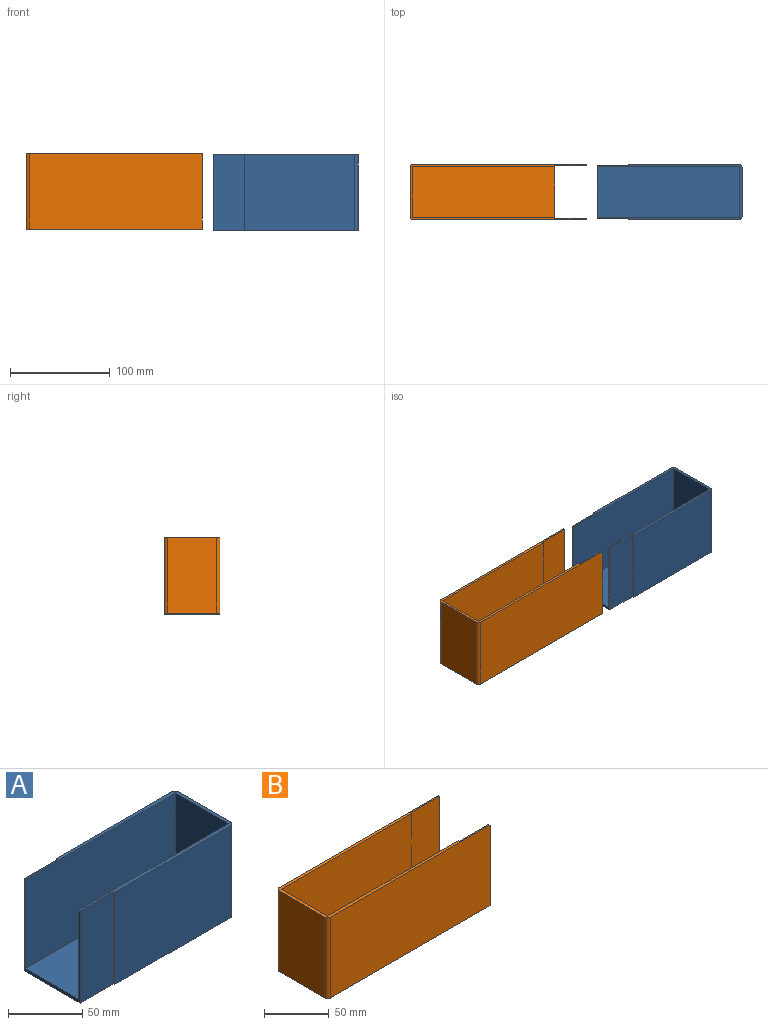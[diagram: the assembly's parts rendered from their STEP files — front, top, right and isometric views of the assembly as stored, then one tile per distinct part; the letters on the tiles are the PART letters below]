
ASSEMBLY  parts=2 mates=2
PART A: 16 faces, bbox 145.4x55.9x76.2 mm
  f0: plane 110.62x76.2mm, normal (0,1,0), area 8429mm2, adj f2,f3,f10,f15
  f1: plane 110.62x76.2mm, normal (0,-1,0), area 8429mm2, adj f2,f3,f11,f14
  f2: plane 145.42x55.88mm, normal (0,0,1), area 781.5mm2, adj f0,f1,f4,f5,f7,f8,f9,f10
  f3: plane 145.42x55.88mm, normal (0,0,-1), area 8039.5mm2, adj f0,f1,f7,f9,f10,f11,f12,f13
  f4: plane 142.88x73.66mm, normal (0,-1,0), area 10524.2mm2, adj f2,f6,f8,f13
  f5: plane 142.88x73.66mm, normal (0,1,0), area 10524.2mm2, adj f2,f6,f8,f13
  f6: plane 142.88x50.8mm, normal (0,0,1), area 7258mm2, adj f4,f5,f8,f13
  f7: plane 76.2x49.78mm, normal (1,0,0), area 3793.5mm2, adj f2,f3,f14,f15
  f8: plane 73.66x50.8mm, normal (-1,0,0), area 3741.9mm2, adj f2,f4,f5,f6
  f9: plane 76.2x31.75mm, normal (0,1,0), area 2419.3mm2, adj f2,f3,f10,f13
  f10: plane 76.2x1.32mm, normal (-1,0,0), area 100.6mm2, adj f0,f2,f3,f9
  f11: plane 76.2x1.27mm, normal (-1,0,0), area 96.8mm2, adj f1,f2,f3,f12
  f12: plane 76.2x31.75mm, normal (0,-1,0), area 2419.3mm2, adj f2,f3,f11,f13
  f13: plane 76.2x53.29mm, normal (-1,0,0), area 318.7mm2, adj f2,f3,f4,f5,f6,f9,f12
  f14: cylinder r=3.05mm len=76.2mm, axis (0,0,1), area 364.8mm2, adj f1,f2,f3,f7
  f15: cylinder r=3.05mm len=76.2mm, axis (0,0,-1), area 364.8mm2, adj f0,f2,f3,f7
PART B: 16 faces, bbox 177.2x55.9x76.2 mm
  f0: plane 177.17x55.88mm, normal (0,0,1), area 944.4mm2, adj f1,f2,f3,f5,f6,f7,f9,f10
  f1: plane 174.12x76.2mm, normal (0,1,0), area 13267.7mm2, adj f0,f4,f9,f14
  f2: plane 76.2x49.78mm, normal (-1,0,0), area 3793.5mm2, adj f0,f4,f14,f15
  f3: plane 174.12x76.2mm, normal (0,-1,0), area 13267.7mm2, adj f0,f4,f12,f15
  f4: plane 177.17x55.88mm, normal (0,0,-1), area 8202.4mm2, adj f1,f2,f3,f9,f10,f11,f12,f13
  f5: plane 142.88x73.66mm, normal (0,-1,0), area 10524.2mm2, adj f0,f6,f8,f13
  f6: plane 73.66x50.8mm, normal (1,0,0), area 3741.9mm2, adj f0,f5,f7,f8
  f7: plane 142.88x73.66mm, normal (0,1,0), area 10524.2mm2, adj f0,f6,f8,f13
  f8: plane 142.88x50.8mm, normal (0,0,1), area 7258mm2, adj f5,f6,f7,f13
  f9: plane 76.2x1.27mm, normal (1,0,0), area 96.8mm2, adj f0,f1,f4,f10
  f10: plane 76.2x31.75mm, normal (0,-1,0), area 2419.3mm2, adj f0,f4,f9,f13
  f11: plane 76.2x31.75mm, normal (0,1,0), area 2419.3mm2, adj f0,f4,f12,f13
  f12: plane 76.2x1.27mm, normal (1,0,0), area 96.8mm2, adj f0,f3,f4,f11
  f13: plane 76.2x53.34mm, normal (1,0,0), area 322.6mm2, adj f0,f4,f5,f7,f8,f10,f11
  f14: cylinder r=3.05mm len=76.2mm, axis (0,0,1), area 364.8mm2, adj f0,f1,f2,f4
  f15: cylinder r=3.05mm len=76.2mm, axis (0,0,-1), area 364.8mm2, adj f0,f2,f3,f4
PLACE A t=(90.94,-46.76,-12.18)mm
PLACE B t=(48.17,-46.81,-10.55)mm
MATE parallel A.f12 <-> B.f11  axis (0,-1,0) through (106.82,-73.43,25.92)mm
MATE planar A.f9 <-> B.f10  axis (0,1,0) through (106.82,-20.14,25.92)mm
